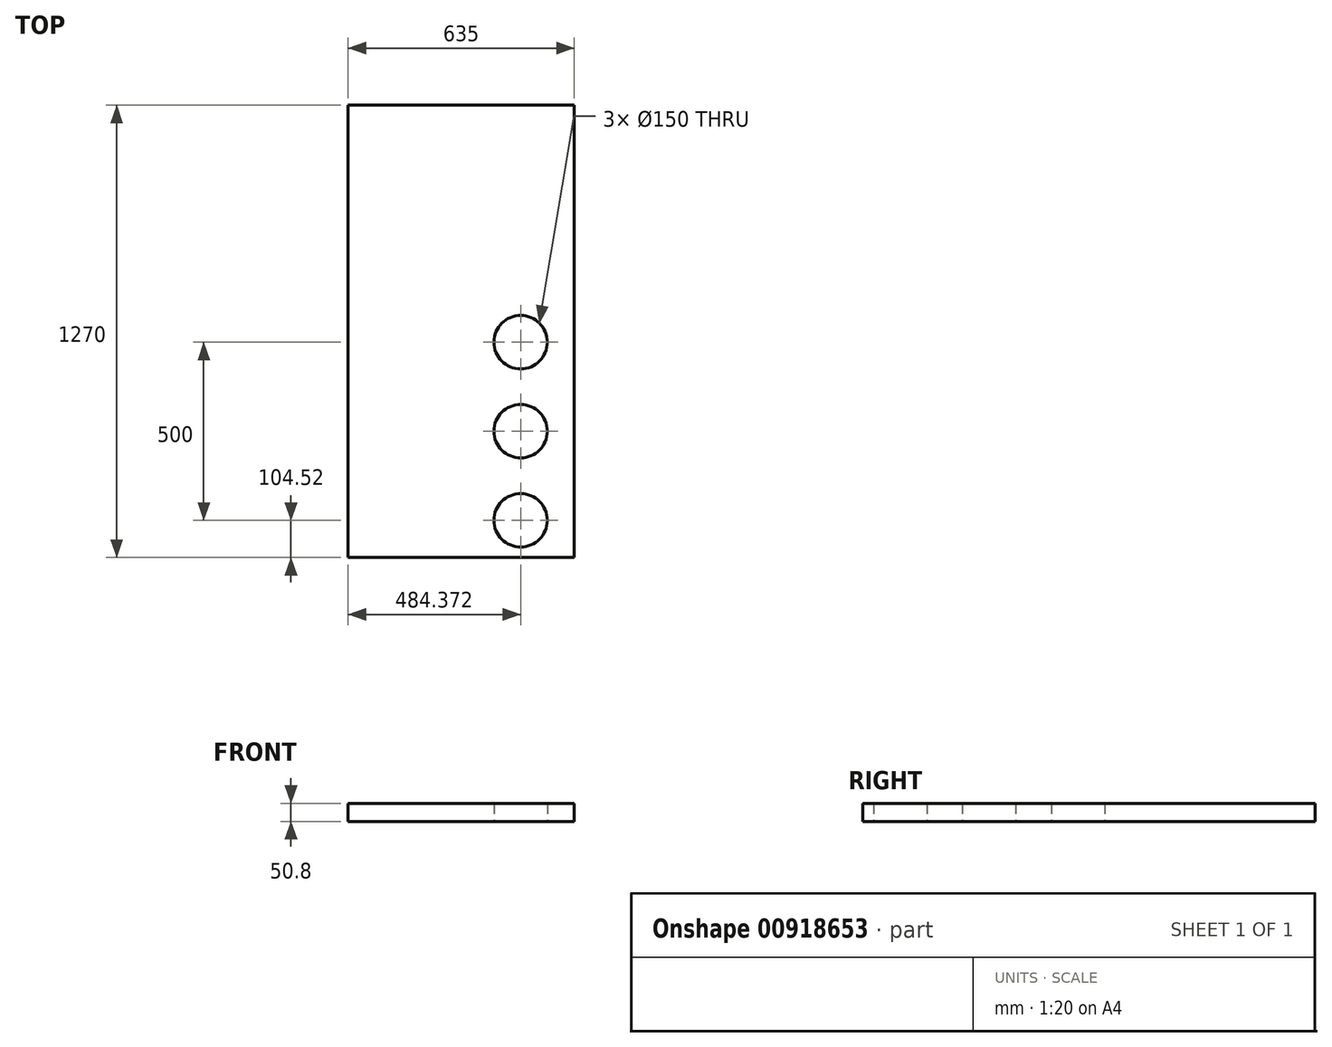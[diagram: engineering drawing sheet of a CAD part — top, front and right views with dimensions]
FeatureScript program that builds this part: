
annotation { "Feature Type Name" : "Feature", "Feature Type Description" : "" }
export const myFeature = defineFeature(function(context is Context, id is Id, definition is map)
    precondition{}
    {
        {
            var Q0;
            Q0=qCreatedBy(makeId("Top.planeOp"),FACE);
            var sketch = newSketch(context, id + "F0", { "sketchPlane" : qUnion([Q0])});
            skLineSegment(sketch, "E0.bottom", {"start": v(453.87, -354.52) * mm, "end": v(-181.13, -354.52) * mm});
            skLineSegment(sketch, "E0.top", {"start": v(453.87, 915.48) * mm, "end": v(-181.13, 915.48) * mm});
            skLineSegment(sketch, "E0.left", {"start": v(453.87, -354.52) * mm, "end": v(453.87, 915.48) * mm});
            skLineSegment(sketch, "E0.right", {"start": v(-181.13, -354.52) * mm, "end": v(-181.13, 915.48) * mm});
            skSolve(sketch);
        }
        {
            var Q0;
            Q0=makeQuery(id+"F0.imprint","IMPRINT",FACE,{"disambiguationData":[TD([[makeQuery(id+"F0.imprint","IMPRINT",EDGE,{"derivedFrom":sQuery(id+"F0.wireOp",EDGE,"E0.bottom")}),-1.0]])]});
            extrude(context, id + "F1", {"entities" : qUnion([Q0]), "depth" : 50.8 * mm, "offsetDistance" : 25.4 * mm});
        }
        {
            var Q0;
            Q0=makeQuery(id+"F1.opExtrude","CAP_FACE",FACE,{"disambiguationData":[OSD([sQuery(id+"F0.wireOp",EDGE,"E0.bottom"),sQuery(id+"F0.wireOp",EDGE,"E0.top"),sQuery(id+"F0.wireOp",EDGE,"E0.left"),sQuery(id+"F0.wireOp",EDGE,"E0.right")])],"isStart":true});
            var sketch = newSketch(context, id + "F2", { "sketchPlane" : qUnion([Q0])});
            skCircle(sketch, "E1", {"center": v(303.24, 250) * mm, "radius": 75 * mm});
            skCircle(sketch, "E2", {"center": v(303.24, 0) * mm, "radius": 75 * mm});
            skCircle(sketch, "E3", {"center": v(303.24, -250) * mm, "radius": 75 * mm});
            skSolve(sketch);
        }
        {
            var Q0;
            Q0 = qSketchRegion(id + "F2", true);
            extrude(context, id + "F3", {"entities" : qUnion([Q0]), "operationType" : NewBodyOperationType.REMOVE, "oppositeDirection" : true, "depth" : 347 * mm, "offsetDistance" : 25 * mm});
        }
    });
